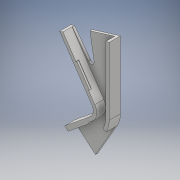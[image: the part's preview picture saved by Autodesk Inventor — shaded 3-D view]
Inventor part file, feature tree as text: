
AUTODESK INVENTOR PART (.ipt)
format: ipt  version: 2017 (Build 210142000, 142)  size: 188,928 bytes
history: native  units: mm
features: extrude x5, sketch x4, chamfer x1
ambient origin geometry x8: Origin, YZ Plane, XZ Plane, XY Plane, X Axis, Y Axis, Z Axis, Center Point
bodies: Solid1 (feature_tree)
feature tree (10):
  sketch  "Sketch1"  dims[d0=38.0mm d1=13.0mm d2=9.0mm d3=5.0mm d4=30.0deg d5=23.0mm d6=6.0mm d7=4.0mm d8=38.0mm d9=30.0deg d10=23.0mm d11=6.0mm d12=4.0mm d13=1.5mm]
  extrude  "Extrusion1"  Depth=1.5mm
  extrude  "Extrusion2"  Depth=1.5mm
  extrude  "Extrusion4"  Depth=12.730996mm
  extrude  "Extrusion5"  Depth=2.0mm
  chamfer  "Chamfer1"  Distance=15.0mm
  extrude  "Extrusion6"  Depth=1.0mm TaperAngle=0.0deg
  sketch  "Sketch2"  dims[d14=1.5mm d15=13.885952mm]
  sketch  "Sketch3"  dims[d16=13.885952mm d17=12.730996mm]
  sketch  "Sketch4"  dims[d18=12.730996mm d19=30.0mm d20=15.0mm d21=1.0mm d22=0.0mm d23=4.0mm d24=0.0mm d28=12.0mm d29=0.5mm d30=0.0mm d31=10.0mm d32=5.0mm d33=1.0mm d34=0.5mm d35=0.0mm d36=0.25mm d37=2.0mm d38=45.0deg d39=10.0mm d40=0.0mm d42=2.0mm]
